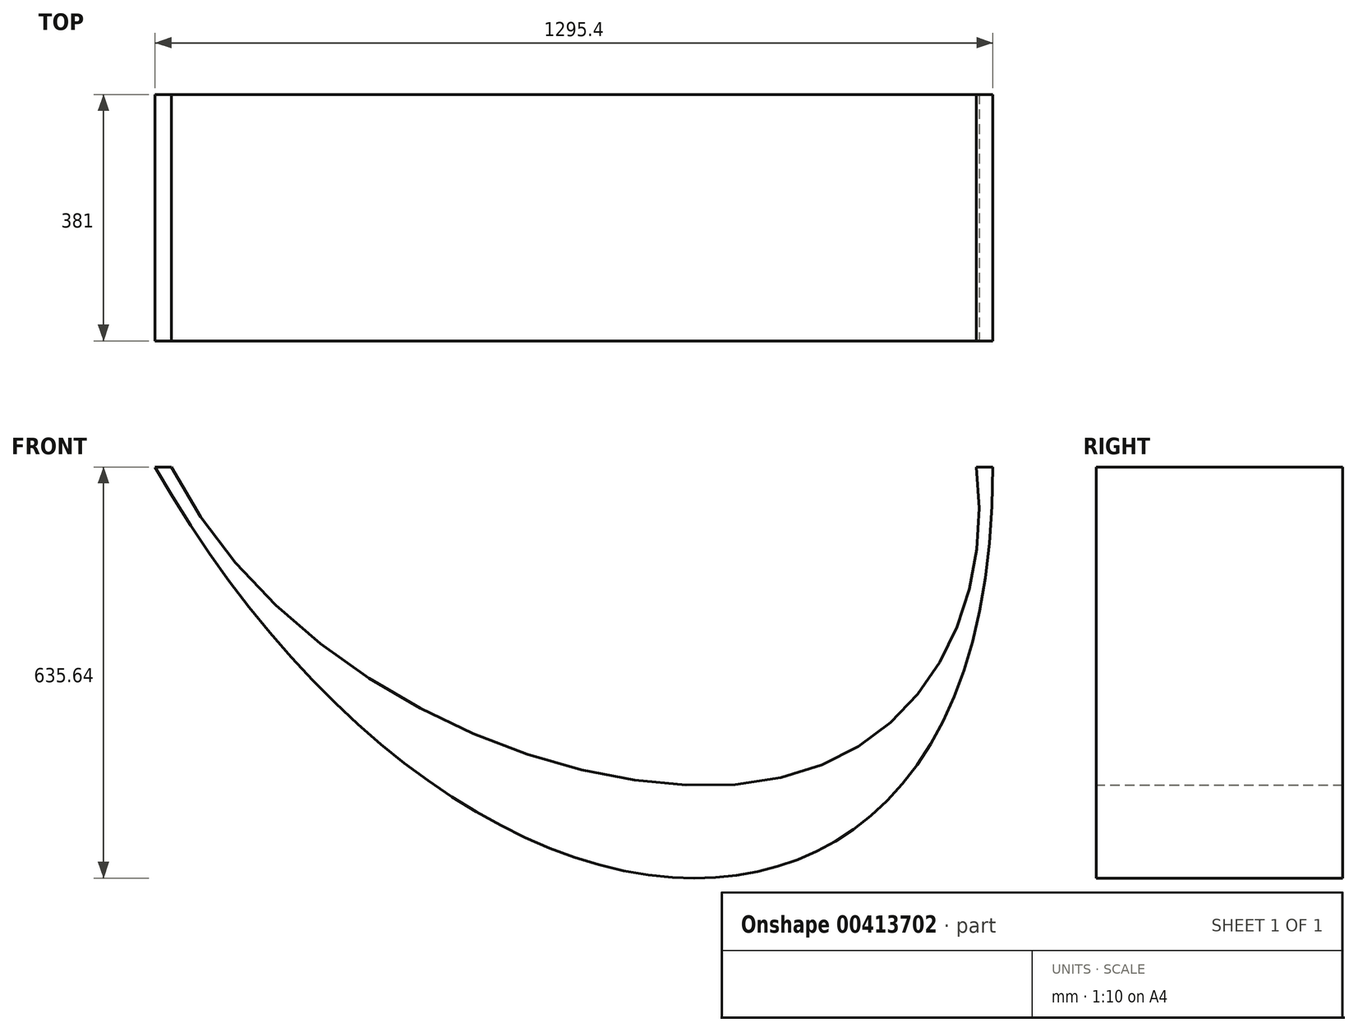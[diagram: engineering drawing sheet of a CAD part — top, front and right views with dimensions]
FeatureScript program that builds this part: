
annotation { "Feature Type Name" : "Feature", "Feature Type Description" : "" }
export const myFeature = defineFeature(function(context is Context, id is Id, definition is map)
    precondition{}
    {
        {
            var Q0;
            Q0=qCreatedBy(makeId("Front.planeOp"),FACE);
            var sketch = newSketch(context, id + "F0", { "sketchPlane" : qUnion([Q0])});
            skLineSegment(sketch, "E0.bottom", {"start": v(-1206.5, 0) * mm, "end": v(952.5, 0) * mm, "construction": true});
            skLineSegment(sketch, "E0.top", {"start": v(-1206.5, -711.2) * mm, "end": v(952.5, -711.2) * mm, "construction": true});
            skLineSegment(sketch, "E0.left", {"start": v(-1206.5, 0) * mm, "end": v(-1206.5, -711.2) * mm, "construction": true});
            skLineSegment(sketch, "E0.right", {"start": v(952.5, 0) * mm, "end": v(952.5, -711.2) * mm, "construction": true});
            skLineSegment(sketch, "E1", {"start": v(-800.1, 0) * mm, "end": v(-800.1, -711.2) * mm, "construction": true});
            skLineSegment(sketch, "E2", {"start": v(495.3, 0) * mm, "end": v(495.3, -711.2) * mm, "construction": true});
            skLineSegment(sketch, "E3", {"start": v(0, 0) * mm, "end": v(0, -711.2) * mm, "construction": true});
            skLineSegment(sketch, "E4", {"start": v(304.8, -635) * mm, "end": v(304.8, -711.2) * mm, "construction": true});
            skLineSegment(sketch, "E5", {"start": v(-304.8, -635) * mm, "end": v(-304.8, -711.2) * mm, "construction": true});
            skFitSpline(sketch, "E6", {"points": [v(-800.1, 0) * mm, v(0, -634.51) * mm, v(495.3, 0) * mm], "startDerivative": vector(1137.76, -2013.95) * mm, "endDerivative": vector(0, 3053.9) * mm});
            skPoint(sketch, "E7", {"position": v(-800.1, -355.6) * mm});
            skFitSpline(sketch, "E8", {"points": [v(-774.7, 0) * mm, v(195.94, -472.96) * mm, v(469.9, 0) * mm], "startDerivative": vector(901.06, -1825.81) * mm, "endDerivative": vector(-183.3, 1473.03) * mm});
            skLineSegment(sketch, "E9", {"start": v(-800.1, 0) * mm, "end": v(-774.7, 0) * mm});
            skLineSegment(sketch, "E10", {"start": v(469.9, 0) * mm, "end": v(495.3, 0) * mm});
            skLineSegment(sketch, "E11", {"start": v(50.8, 0) * mm, "end": v(50.8, -632.16) * mm, "construction": true});
            skLineSegment(sketch, "E12.right", {"start": v(0, -634.51) * mm, "end": v(0, -632.16) * mm});
            skLineSegment(sketch, "E13", {"start": v(50.8, 0) * mm, "end": v(50.8, -711.2) * mm, "construction": true});
            skLineSegment(sketch, "E14.left", {"start": v(204.61, -632.16) * mm, "end": v(204.61, -632.16) * mm});
            skLineSegment(sketch, "E14.right", {"start": v(-103.01, -632.16) * mm, "end": v(-103.01, -632.16) * mm});
            skPoint(sketch, "E14.middle", {"position": v(50.8, -632.16) * mm});
            skSolve(sketch);
        }
        {
            var Q0;
            Q0=makeQuery(id+"F0.imprint","IMPRINT",FACE,{"disambiguationData":[TD([[makeQuery(id+"F0.imprint","IMPRINT",EDGE,{"derivedFrom":sQuery(id+"F0.wireOp",EDGE,"E6")}),1.0]])]});
            extrude(context, id + "F1", {"entities" : qUnion([Q0]), "depth" : 381 * mm});
        }
    });
